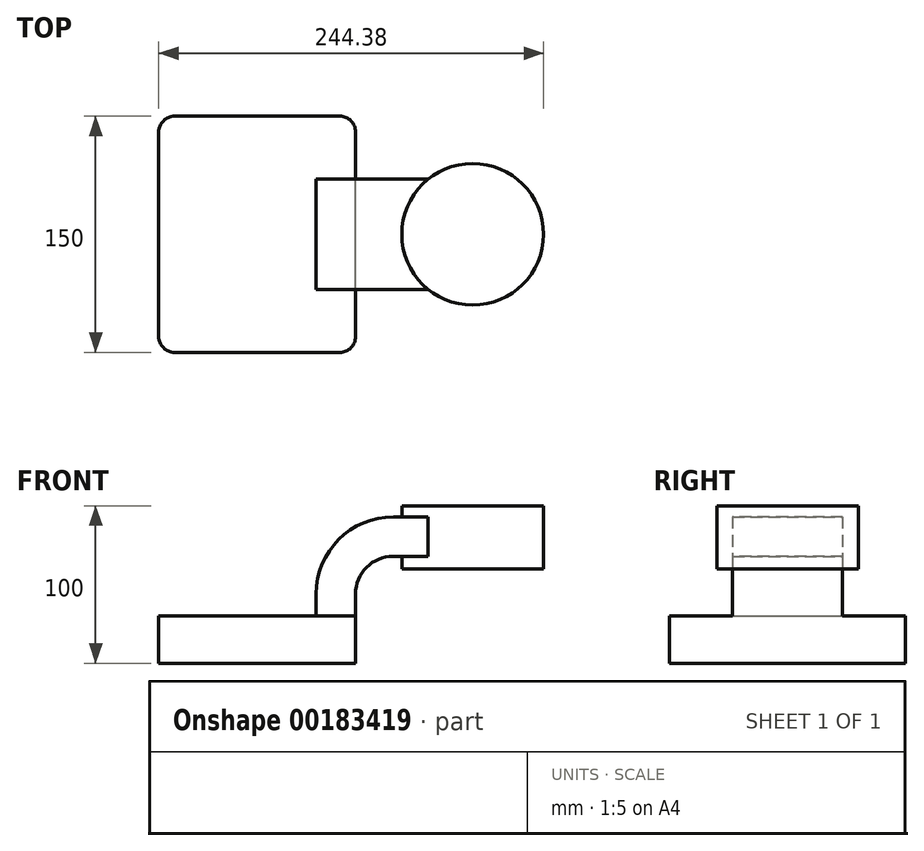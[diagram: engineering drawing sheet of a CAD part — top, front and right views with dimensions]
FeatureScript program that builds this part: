
annotation { "Feature Type Name" : "Feature", "Feature Type Description" : "" }
export const myFeature = defineFeature(function(context is Context, id is Id, definition is map)
    precondition{}
    {
        {
            var Q0;
            Q0=qCreatedBy(makeId("Front.planeOp"),FACE);
            var sketch = newSketch(context, id + "F0", { "sketchPlane" : qUnion([Q0])});
            skLineSegment(sketch, "E0.bottom", {"start": v(62.5, -15) * mm, "end": v(-62.5, -15) * mm});
            skLineSegment(sketch, "E0.top", {"start": v(62.5, 15) * mm, "end": v(-62.5, 15) * mm});
            skLineSegment(sketch, "E0.left", {"start": v(62.5, -15) * mm, "end": v(62.5, 15) * mm});
            skLineSegment(sketch, "E0.right", {"start": v(-62.5, -15) * mm, "end": v(-62.5, 15) * mm});
            skPoint(sketch, "E0.middle", {"position": v(0, 0) * mm});
            skLineSegment(sketch, "E1.bottom", {"start": v(181.87, 45) * mm, "end": v(91.87, 45) * mm});
            skLineSegment(sketch, "E1.top", {"start": v(181.87, 85) * mm, "end": v(91.87, 85) * mm});
            skLineSegment(sketch, "E1.left", {"start": v(181.87, 45) * mm, "end": v(181.87, 85) * mm});
            skLineSegment(sketch, "E1.right", {"start": v(91.87, 45) * mm, "end": v(91.87, 85) * mm});
            skPoint(sketch, "E1.middle", {"position": v(136.87, 65) * mm});
            skLineSegment(sketch, "E2", {"start": v(62.5, 15) * mm, "end": v(62.5, 29) * mm});
            skArc(sketch, "E3", {"start": v(62.5, 29) * mm, "mid": v(69.53, 45.97) * mm, "end": v(86.5, 53) * mm});
            skLineSegment(sketch, "E4", {"start": v(86.5, 53) * mm, "end": v(137.64, 53) * mm});
            skLineSegment(sketch, "E5.0", {"start": v(86.5, 78) * mm, "end": v(136.87, 78) * mm});
            skArc(sketch, "E5.1", {"start": v(37.5, 29) * mm, "mid": v(51.85, 63.65) * mm, "end": v(86.5, 78) * mm});
            skLineSegment(sketch, "E5.2", {"start": v(37.5, 15) * mm, "end": v(37.5, 29) * mm});
            skLineSegment(sketch, "E6", {"start": v(136.87, 85) * mm, "end": v(136.87, 45) * mm});
            skFitSpline(sketch, "E7", {"points": [v(-62.5, 15) * mm, v(86.5, 78) * mm], "startDerivative": vector(68.13, 123.2) * mm, "endDerivative": vector(259.5, -9.33) * mm});
            skSolve(sketch);
        }
        {
            var Q0;
            Q0=makeQuery(id+"F0.imprint","IMPRINT",FACE,{"disambiguationData":[TD([[makeQuery(id+"F0.imprint","IMPRINT",EDGE,{"derivedFrom":sQuery(id+"F0.wireOp",EDGE,"E0.bottom")}),-1.0]])]});
            extrude(context, id + "F1", {"entities" : qUnion([Q0]), "endBound" : BoundingType.SYMMETRIC, "depth" : 150 * mm});
        }
        {
            var Q0;
            Q0=makeQuery(id+"F0.imprint","IMPRINT",FACE,{"disambiguationData":[TD([[makeQuery(id+"F0.imprint","IMPRINT",EDGE,{"derivedFrom":sQuery(id+"F0.wireOp",EDGE,"E5.1")}),1.0]])]});
            extrude(context, id + "F2", {"entities" : qUnion([Q0]), "operationType" : NewBodyOperationType.ADD, "endBound" : BoundingType.SYMMETRIC, "depth" : 20 * mm});
        }
        {
            var Q0;
            {var subQ1=sQuery(id+"F0.wireOp",EDGE,"E2");Q0=makeQuery(id+"F0.imprint","IMPRINT",FACE,{"disambiguationData":[TD([[makeQuery(id+"F0.imprint","IMPRINT",EDGE,{"derivedFrom":subQ1}),1.0]])]});}
            var Q1;
            {var subQ0=sQuery(id+"F0.wireOp",EDGE,"E4");var subQ1=sQuery(id+"F0.wireOp",EDGE,"E1.right");var subQ2=makeQuery(id+"F0.imprint","INTERSECT",VERTEX,{"derivedFrom":[subQ1,subQ0]});Q1=makeQuery(id+"F0.imprint","IMPRINT",FACE,{"disambiguationData":[TD([[makeQuery(id+"F0.imprint","IMPRINT",EDGE,{"disambiguationData":[TD([[subQ2,-1.0]])],"derivedFrom":subQ1}),-1.0]])]});}
            extrude(context, id + "F3", {"entities" : qUnion([Q0, Q1]), "operationType" : NewBodyOperationType.ADD, "endBound" : BoundingType.SYMMETRIC, "oppositeDirection" : true, "depth" : 70 * mm});
        }
        {
            var Q0;
            {var subQ0=sQuery(id+"F0.wireOp",EDGE,"E1.left");Q0=makeQuery(id+"F0.imprint","IMPRINT",FACE,{"disambiguationData":[TD([[makeQuery(id+"F0.imprint","IMPRINT",EDGE,{"derivedFrom":subQ0}),1.0]])]});}
            var Q1;
            Q1=sQuery(id+"F0.wireOp",EDGE,"E6");
            revolve(context, id + "F4", {"operationType" : NewBodyOperationType.ADD, "entities" : qUnion([Q0]), "axis" : qUnion([Q1]), "revolveType" : RevolveType.SYMMETRIC, "oppositeDirection" : true, "angle" : 6.28 * radian});
        }
        {
            var Q0;
            Q0=makeQuery(id+"F1.opExtrude","CAP_EDGE",EDGE,{"disambiguationData":[OSD([sQuery(id+"F0.wireOp",EDGE,"E0.left")])],"isStart":false});
            var Q1;
            Q1=makeQuery(id+"F1.opExtrude","CAP_EDGE",EDGE,{"disambiguationData":[OSD([sQuery(id+"F0.wireOp",EDGE,"E0.right")])],"isStart":false});
            var Q2;
            Q2=makeQuery(id+"F1.opExtrude","CAP_EDGE",EDGE,{"disambiguationData":[OSD([sQuery(id+"F0.wireOp",EDGE,"E0.right")])],"isStart":true});
            var Q3;
            Q3=makeQuery(id+"F1.opExtrude","CAP_EDGE",EDGE,{"disambiguationData":[OSD([sQuery(id+"F0.wireOp",EDGE,"E0.left")])],"isStart":true});
            fillet(context, id + "F5", {"entities" : qUnion([Q0, Q1, Q2, Q3]), "radius" : 10 * mm, "tangentPropagation" : true, "allowEdgeOverflow" : false});
        }
    });
